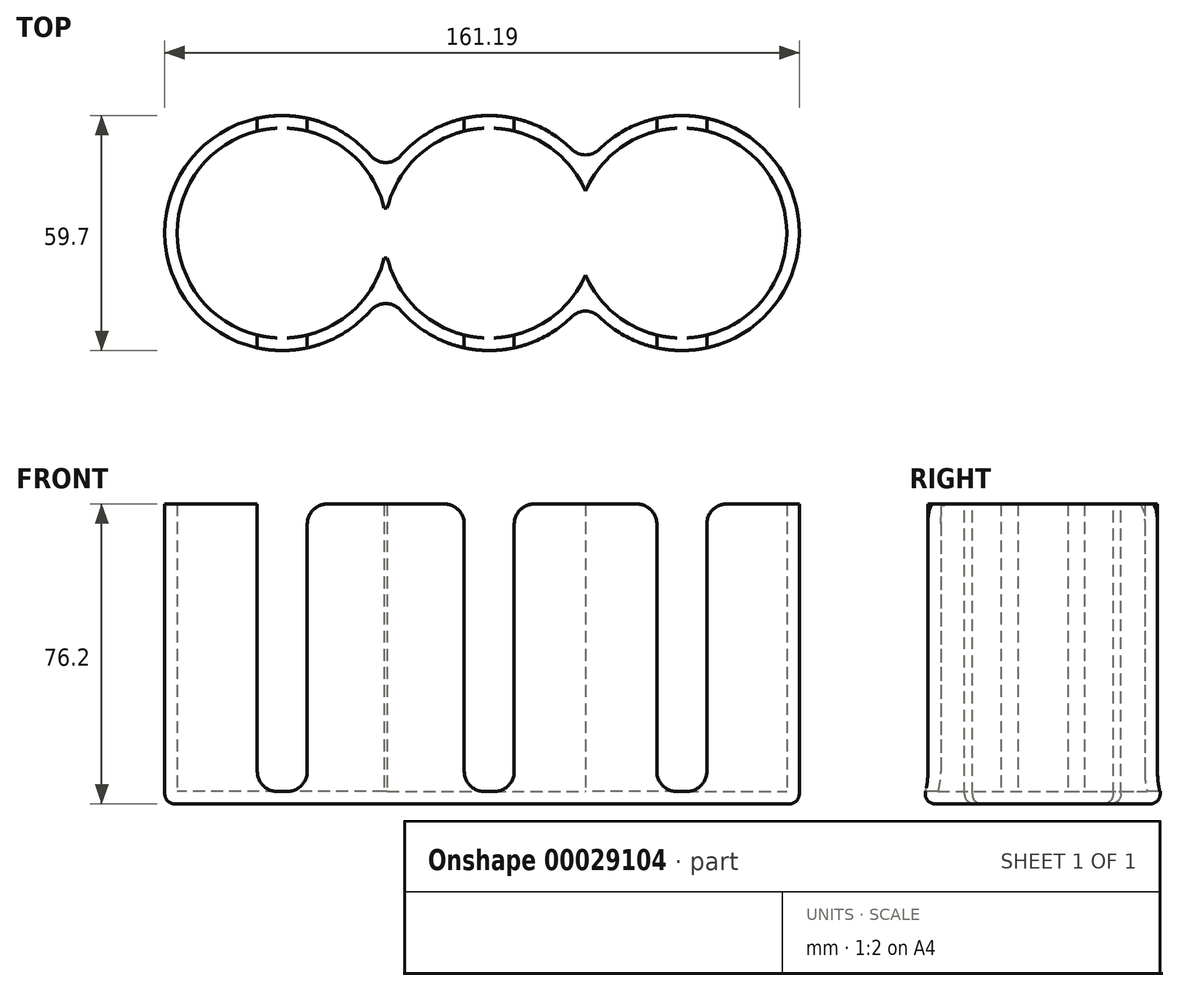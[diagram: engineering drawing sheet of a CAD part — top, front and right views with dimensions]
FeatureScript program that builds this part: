
annotation { "Feature Type Name" : "Feature", "Feature Type Description" : "" }
export const myFeature = defineFeature(function(context is Context, id is Id, definition is map)
    precondition{}
    {
        {
            var Q0;
            Q0=qCreatedBy(makeId("Top.planeOp"),FACE);
            var sketch = newSketch(context, id + "F0", { "sketchPlane" : qUnion([Q0])});
            skPoint(sketch, "E0.center.orphan", {"position": v(-35.14, 0) * mm});
            skPoint(sketch, "E1.center.orphan", {"position": v(35.14, 0) * mm});
            skPoint(sketch, "E2.center.orphan", {"position": v(0, 0) * mm});
            skArc(sketch, "E3", {"start": v(-26.3, 14.12) * mm, "mid": v(-82.43, 0) * mm, "end": v(-26.3, -14.12) * mm});
            skArc(sketch, "E4", {"start": v(-26.3, -14.12) * mm, "mid": v(-1.75, -29.8) * mm, "end": v(24.46, -17.1) * mm});
            skArc(sketch, "E5", {"start": v(24.46, -17.1) * mm, "mid": v(78.76, 0) * mm, "end": v(24.46, 17.1) * mm});
            skArc(sketch, "E6.trimOffspring", {"start": v(24.46, 17.1) * mm, "mid": v(-1.75, 29.8) * mm, "end": v(-26.3, 14.12) * mm});
            skSolve(sketch);
        }
        {
            var Q0;
            Q0 = qSketchRegion(id + "F0", true);
            extrude(context, id + "F1", {"entities" : qUnion([Q0]), "depth" : 76.2 * mm});
        }
        {
            var Q0;
            Q0=makeQuery(id+"F1.opExtrude","CAP_FACE",FACE,{"disambiguationData":[OSD([sQuery(id+"F0.wireOp",EDGE,"E3"),sQuery(id+"F0.wireOp",EDGE,"E4"),sQuery(id+"F0.wireOp",EDGE,"E5"),sQuery(id+"F0.wireOp",EDGE,"E6.trimOffspring")])],"isStart":false});
            shell(context, id + "F2", {"entities" : qUnion([Q0]), "thickness" : 3.17 * mm});
        }
        {
            var Q0;
            Q0=makeQuery(id+"F1.opExtrude","CAP_FACE",FACE,{"disambiguationData":[OSD([sQuery(id+"F0.wireOp",EDGE,"E3"),sQuery(id+"F0.wireOp",EDGE,"E4"),sQuery(id+"F0.wireOp",EDGE,"E5"),sQuery(id+"F0.wireOp",EDGE,"E6.trimOffspring")])],"isStart":false});
            var sketch = newSketch(context, id + "F3", { "sketchPlane" : qUnion([Q0])});
            skLineSegment(sketch, "E7.rect.bottom", {"start": v(35.34, 6.35) * mm, "end": v(-35.34, 6.35) * mm});
            skLineSegment(sketch, "E7.rect.top", {"start": v(35.34, -6.35) * mm, "end": v(-35.34, -6.35) * mm});
            skLineSegment(sketch, "E7.rect.left", {"start": v(35.34, 6.35) * mm, "end": v(35.34, -6.35) * mm});
            skLineSegment(sketch, "E7.rect.right", {"start": v(-35.34, 6.35) * mm, "end": v(-35.34, -6.35) * mm});
            skPoint(sketch, "E7.rect.middle", {"position": v(0, 0) * mm});
            skSolve(sketch);
        }
        {
            var Q0;
            Q0 = qSketchRegion(id + "F3", true);
            extrude(context, id + "F4", {"entities" : qUnion([Q0]), "operationType" : NewBodyOperationType.REMOVE, "oppositeDirection" : true, "depth" : 73.03 * mm});
        }
        {
            var Q0;
            Q0=makeQuery(id+"F1.opExtrude","CAP_FACE",FACE,{"disambiguationData":[OSD([sQuery(id+"F0.wireOp",EDGE,"E3"),sQuery(id+"F0.wireOp",EDGE,"E4"),sQuery(id+"F0.wireOp",EDGE,"E5"),sQuery(id+"F0.wireOp",EDGE,"E6.trimOffspring")])],"isStart":false});
            var sketch = newSketch(context, id + "F5", { "sketchPlane" : qUnion([Q0])});
            skArc(sketch, "E8.0", {"start": v(-26.68, 6.35) * mm, "mid": v(-79.26, 0) * mm, "end": v(-26.68, -6.35) * mm, "construction": true});
            skLineSegment(sketch, "E9.0", {"start": v(-25.9, 6.35) * mm, "end": v(-25.9, 6.35) * mm});
            skLineSegment(sketch, "E10.rect.bottom", {"start": v(-46.23, 31.7) * mm, "end": v(-58.93, 31.7) * mm});
            skLineSegment(sketch, "E10.rect.top", {"start": v(-46.23, -31.7) * mm, "end": v(-58.93, -31.7) * mm});
            skLineSegment(sketch, "E10.rect.left", {"start": v(-46.23, 31.7) * mm, "end": v(-46.23, -31.7) * mm});
            skLineSegment(sketch, "E10.rect.right", {"start": v(-58.93, 31.7) * mm, "end": v(-58.93, -31.7) * mm});
            skLineSegment(sketch, "E11.rect.bottom", {"start": v(6.35, 30.58) * mm, "end": v(-6.35, 30.58) * mm});
            skLineSegment(sketch, "E11.rect.top", {"start": v(6.35, -30.58) * mm, "end": v(-6.35, -30.58) * mm});
            skLineSegment(sketch, "E11.rect.left", {"start": v(6.35, 30.58) * mm, "end": v(6.35, -30.58) * mm});
            skLineSegment(sketch, "E11.rect.right", {"start": v(-6.35, 30.58) * mm, "end": v(-6.35, -30.58) * mm});
            skLineSegment(sketch, "E12.rect.bottom", {"start": v(55.27, 30.25) * mm, "end": v(42.57, 30.25) * mm});
            skLineSegment(sketch, "E12.rect.top", {"start": v(55.27, -30.25) * mm, "end": v(42.57, -30.25) * mm});
            skLineSegment(sketch, "E12.rect.left", {"start": v(55.27, 30.25) * mm, "end": v(55.27, -30.25) * mm});
            skLineSegment(sketch, "E12.rect.right", {"start": v(42.57, 30.25) * mm, "end": v(42.57, -30.25) * mm});
            skPoint(sketch, "E12.rect.middle", {"position": v(48.92, 0) * mm});
            skArc(sketch, "E13.0", {"start": v(24.46, -10.64) * mm, "mid": v(75.59, 0) * mm, "end": v(24.46, 10.64) * mm, "construction": true});
            skArc(sketch, "E14.0", {"start": v(24.46, 10.64) * mm, "mid": v(-2.26, 26.58) * mm, "end": v(-25.9, 6.35) * mm, "construction": true});
            skArc(sketch, "E15.0", {"start": v(-25.9, -6.35) * mm, "mid": v(-2.26, -26.58) * mm, "end": v(24.46, -10.64) * mm, "construction": true});
            skSolve(sketch);
        }
        {
            var Q0;
            Q0 = qSketchRegion(id + "F5", true);
            extrude(context, id + "F6", {"entities" : qUnion([Q0]), "operationType" : NewBodyOperationType.REMOVE, "oppositeDirection" : true, "depth" : 73.03 * mm});
        }
        {
            var Q0;
            Q0=makeQuery(id+"F1.opExtrude","SWEPT_EDGE",EDGE,{"disambiguationData":[OSD([sQuery(id+"F0.wireOp",EDGE,"E3"),sQuery(id+"F0.wireOp",EDGE,"E4")])]});
            var Q1;
            Q1=makeQuery(id+"F1.opExtrude","SWEPT_EDGE",EDGE,{"disambiguationData":[OSD([sQuery(id+"F0.wireOp",EDGE,"E4"),sQuery(id+"F0.wireOp",EDGE,"E5")])]});
            var Q2;
            Q2=makeQuery(id+"F1.opExtrude","SWEPT_EDGE",EDGE,{"disambiguationData":[OSD([sQuery(id+"F0.wireOp",EDGE,"E5"),sQuery(id+"F0.wireOp",EDGE,"E6.trimOffspring")])]});
            var Q3;
            Q3=makeQuery(id+"F1.opExtrude","SWEPT_EDGE",EDGE,{"disambiguationData":[OSD([sQuery(id+"F0.wireOp",EDGE,"E3"),sQuery(id+"F0.wireOp",EDGE,"E6.trimOffspring")])]});
            var Q4;
            Q4=makeQuery(id+"F6.boolean.opBoolean","COPY",EDGE,{"disambiguationData":[OD(0.0)],"derivedFrom":makeQuery(id+"F6.opExtrude","CAP_EDGE",EDGE,{"disambiguationData":[OSD([sQuery(id+"F5.wireOp",EDGE,"E10.rect.right")])],"isStart":false})});
            var Q5;
            Q5=makeQuery(id+"F6.boolean.opBoolean","COPY",EDGE,{"disambiguationData":[OD(1.0)],"derivedFrom":makeQuery(id+"F6.opExtrude","CAP_EDGE",EDGE,{"disambiguationData":[OSD([sQuery(id+"F5.wireOp",EDGE,"E11.rect.right")])],"isStart":false})});
            var Q6;
            Q6=makeQuery(id+"F6.boolean.opBoolean","COPY",EDGE,{"disambiguationData":[OD(1.0)],"derivedFrom":makeQuery(id+"F6.opExtrude","CAP_EDGE",EDGE,{"disambiguationData":[OSD([sQuery(id+"F5.wireOp",EDGE,"E11.rect.left")])],"isStart":false})});
            var Q7;
            Q7=makeQuery(id+"F6.boolean.opBoolean","COPY",EDGE,{"disambiguationData":[OD(0.0)],"derivedFrom":makeQuery(id+"F6.opExtrude","CAP_EDGE",EDGE,{"disambiguationData":[OSD([sQuery(id+"F5.wireOp",EDGE,"E10.rect.left")])],"isStart":false})});
            var Q8;
            Q8=makeQuery(id+"F6.boolean.opBoolean","COPY",EDGE,{"disambiguationData":[OD(0.0)],"derivedFrom":makeQuery(id+"F6.opExtrude","CAP_EDGE",EDGE,{"disambiguationData":[OSD([sQuery(id+"F5.wireOp",EDGE,"E12.rect.left")])],"isStart":false})});
            var Q9;
            Q9=makeQuery(id+"F6.boolean.opBoolean","COPY",EDGE,{"disambiguationData":[OD(0.0)],"derivedFrom":makeQuery(id+"F6.opExtrude","CAP_EDGE",EDGE,{"disambiguationData":[OSD([sQuery(id+"F5.wireOp",EDGE,"E12.rect.right")])],"isStart":false})});
            var Q10;
            Q10=makeQuery(id+"F6.boolean.opBoolean","COPY",EDGE,{"disambiguationData":[OD(1.0)],"derivedFrom":makeQuery(id+"F6.opExtrude","CAP_EDGE",EDGE,{"disambiguationData":[OSD([sQuery(id+"F5.wireOp",EDGE,"E12.rect.left")])],"isStart":false})});
            var Q11;
            Q11=makeQuery(id+"F6.boolean.opBoolean","COPY",EDGE,{"disambiguationData":[OD(0.0)],"derivedFrom":makeQuery(id+"F6.opExtrude","CAP_EDGE",EDGE,{"disambiguationData":[OSD([sQuery(id+"F5.wireOp",EDGE,"E11.rect.left")])],"isStart":false})});
            var Q12;
            Q12=makeQuery(id+"F6.boolean.opBoolean","COPY",EDGE,{"disambiguationData":[OD(1.0)],"derivedFrom":makeQuery(id+"F6.opExtrude","CAP_EDGE",EDGE,{"disambiguationData":[OSD([sQuery(id+"F5.wireOp",EDGE,"E10.rect.left")])],"isStart":false})});
            var Q13;
            Q13=makeQuery(id+"F6.boolean.opBoolean","COPY",EDGE,{"disambiguationData":[OD(0.0)],"derivedFrom":makeQuery(id+"F6.opExtrude","CAP_EDGE",EDGE,{"disambiguationData":[OSD([sQuery(id+"F5.wireOp",EDGE,"E11.rect.right")])],"isStart":false})});
            var Q14;
            Q14=makeQuery(id+"F6.boolean.opBoolean","COPY",EDGE,{"disambiguationData":[OD(1.0)],"derivedFrom":makeQuery(id+"F6.opExtrude","CAP_EDGE",EDGE,{"disambiguationData":[OSD([sQuery(id+"F5.wireOp",EDGE,"E12.rect.right")])],"isStart":false})});
            var Q15;
            Q15=makeQuery(id+"F6.boolean.opBoolean","COPY",EDGE,{"disambiguationData":[OD(1.0)],"derivedFrom":makeQuery(id+"F6.opExtrude","CAP_EDGE",EDGE,{"disambiguationData":[OSD([sQuery(id+"F5.wireOp",EDGE,"E10.rect.right")])],"isStart":false})});
            var Q16;
            Q16=makeQuery(id+"F6.boolean.opBoolean","COPY",EDGE,{"disambiguationData":[OD(1.0)],"derivedFrom":makeQuery(id+"F6.opExtrude","CAP_EDGE",EDGE,{"disambiguationData":[OSD([sQuery(id+"F5.wireOp",EDGE,"E10.rect.left")])],"isStart":true})});
            var Q17;
            Q17=makeQuery(id+"F6.boolean.opBoolean","COPY",EDGE,{"disambiguationData":[OD(1.0)],"derivedFrom":makeQuery(id+"F6.opExtrude","CAP_EDGE",EDGE,{"disambiguationData":[OSD([sQuery(id+"F5.wireOp",EDGE,"E10.rect.right")])],"isStart":true})});
            var Q18;
            Q18=makeQuery(id+"F6.boolean.opBoolean","COPY",EDGE,{"disambiguationData":[OD(0.0)],"derivedFrom":makeQuery(id+"F6.opExtrude","CAP_EDGE",EDGE,{"disambiguationData":[OSD([sQuery(id+"F5.wireOp",EDGE,"E10.rect.left")])],"isStart":true})});
            var Q19;
            Q19=makeQuery(id+"F6.boolean.opBoolean","COPY",EDGE,{"disambiguationData":[OD(0.0)],"derivedFrom":makeQuery(id+"F6.opExtrude","CAP_EDGE",EDGE,{"disambiguationData":[OSD([sQuery(id+"F5.wireOp",EDGE,"E10.rect.right")])],"isStart":true})});
            var Q20;
            Q20=makeQuery(id+"F6.boolean.opBoolean","COPY",EDGE,{"disambiguationData":[OD(0.0)],"derivedFrom":makeQuery(id+"F6.opExtrude","CAP_EDGE",EDGE,{"disambiguationData":[OSD([sQuery(id+"F5.wireOp",EDGE,"E11.rect.right")])],"isStart":true})});
            var Q21;
            Q21=makeQuery(id+"F6.boolean.opBoolean","COPY",EDGE,{"disambiguationData":[OD(0.0)],"derivedFrom":makeQuery(id+"F6.opExtrude","CAP_EDGE",EDGE,{"disambiguationData":[OSD([sQuery(id+"F5.wireOp",EDGE,"E11.rect.left")])],"isStart":true})});
            var Q22;
            Q22=makeQuery(id+"F6.boolean.opBoolean","COPY",EDGE,{"disambiguationData":[OD(0.0)],"derivedFrom":makeQuery(id+"F6.opExtrude","CAP_EDGE",EDGE,{"disambiguationData":[OSD([sQuery(id+"F5.wireOp",EDGE,"E12.rect.right")])],"isStart":true})});
            var Q23;
            Q23=makeQuery(id+"F6.boolean.opBoolean","COPY",EDGE,{"disambiguationData":[OD(0.0)],"derivedFrom":makeQuery(id+"F6.opExtrude","CAP_EDGE",EDGE,{"disambiguationData":[OSD([sQuery(id+"F5.wireOp",EDGE,"E12.rect.left")])],"isStart":true})});
            var Q24;
            Q24=makeQuery(id+"F6.boolean.opBoolean","COPY",EDGE,{"disambiguationData":[OD(1.0)],"derivedFrom":makeQuery(id+"F6.opExtrude","CAP_EDGE",EDGE,{"disambiguationData":[OSD([sQuery(id+"F5.wireOp",EDGE,"E12.rect.left")])],"isStart":true})});
            var Q25;
            Q25=makeQuery(id+"F6.boolean.opBoolean","COPY",EDGE,{"disambiguationData":[OD(1.0)],"derivedFrom":makeQuery(id+"F6.opExtrude","CAP_EDGE",EDGE,{"disambiguationData":[OSD([sQuery(id+"F5.wireOp",EDGE,"E12.rect.right")])],"isStart":true})});
            var Q26;
            Q26=makeQuery(id+"F6.boolean.opBoolean","COPY",EDGE,{"disambiguationData":[OD(1.0)],"derivedFrom":makeQuery(id+"F6.opExtrude","CAP_EDGE",EDGE,{"disambiguationData":[OSD([sQuery(id+"F5.wireOp",EDGE,"E11.rect.left")])],"isStart":true})});
            var Q27;
            Q27=makeQuery(id+"F6.boolean.opBoolean","COPY",EDGE,{"disambiguationData":[OD(1.0)],"derivedFrom":makeQuery(id+"F6.opExtrude","CAP_EDGE",EDGE,{"disambiguationData":[OSD([sQuery(id+"F5.wireOp",EDGE,"E11.rect.right")])],"isStart":true})});
            var Q28;
            Q28=makeQuery(id+"F4.boolean.opBoolean","COPY",EDGE,{"disambiguationData":[OD(0.0)],"derivedFrom":makeQuery(id+"F4.opExtrude","CAP_EDGE",EDGE,{"disambiguationData":[OSD([sQuery(id+"F3.wireOp",EDGE,"E7.rect.bottom")])],"isStart":true})});
            var Q29;
            Q29=makeQuery(id+"F4.boolean.opBoolean","COPY",EDGE,{"disambiguationData":[OD(0.0)],"derivedFrom":makeQuery(id+"F4.opExtrude","CAP_EDGE",EDGE,{"disambiguationData":[OSD([sQuery(id+"F3.wireOp",EDGE,"E7.rect.top")])],"isStart":true})});
            var Q30;
            Q30=makeQuery(id+"F4.boolean.opBoolean","COPY",EDGE,{"disambiguationData":[OD(1.0)],"derivedFrom":makeQuery(id+"F4.opExtrude","CAP_EDGE",EDGE,{"disambiguationData":[OSD([sQuery(id+"F3.wireOp",EDGE,"E7.rect.bottom")])],"isStart":true})});
            var Q31;
            Q31=makeQuery(id+"F4.boolean.opBoolean","COPY",EDGE,{"disambiguationData":[OD(1.0)],"derivedFrom":makeQuery(id+"F4.opExtrude","CAP_EDGE",EDGE,{"disambiguationData":[OSD([sQuery(id+"F3.wireOp",EDGE,"E7.rect.top")])],"isStart":true})});
            fillet(context, id + "F7", {"entities" : qUnion([Q0, Q1, Q2, Q3, Q4, Q5, Q6, Q7, Q8, Q9, Q10, Q11, Q12, Q13, Q14, Q15, Q16, Q17, Q18, Q19, Q20, Q21, Q22, Q23, Q24, Q25, Q26, Q27, Q28, Q29, Q30, Q31]), "radius" : 5.08 * mm, "tangentPropagation" : true, "allowEdgeOverflow" : false});
        }
        {
            var Q0;
            Q0=makeQuery(id+"F1.opExtrude","CAP_EDGE",EDGE,{"disambiguationData":[OSD([sQuery(id+"F0.wireOp",EDGE,"E5")])],"isStart":true});
            fillet(context, id + "F8", {"entities" : qUnion([Q0]), "radius" : 2.54 * mm, "tangentPropagation" : true, "allowEdgeOverflow" : false});
        }
    });
